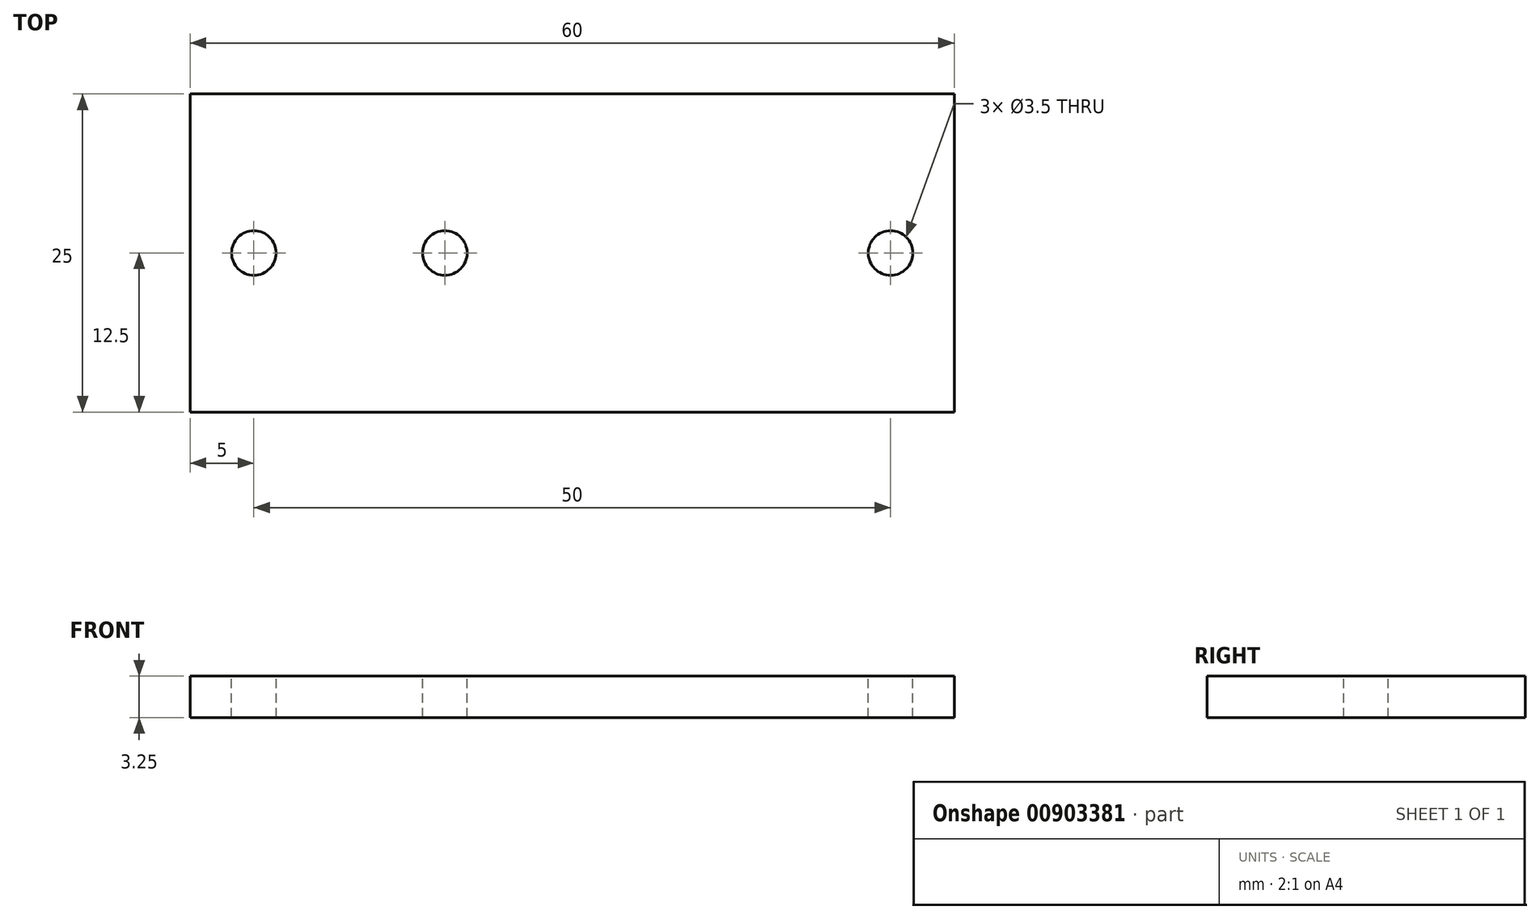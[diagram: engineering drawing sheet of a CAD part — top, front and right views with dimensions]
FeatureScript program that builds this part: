
annotation { "Feature Type Name" : "Feature", "Feature Type Description" : "" }
export const myFeature = defineFeature(function(context is Context, id is Id, definition is map)
    precondition{}
    {
        {
            var Q0;
            Q0=qCreatedBy(makeId("Top.planeOp"), FACE);
            var sketch = newSketch(context, id + "F0", { "sketchPlane" : qUnion([Q0])});
            skLineSegment(sketch, "E0.bottom", {"start": v(0, 0) * mm, "end": v(60, 0) * mm});
            skLineSegment(sketch, "E0.top", {"start": v(0, 25) * mm, "end": v(60, 25) * mm});
            skLineSegment(sketch, "E0.left", {"start": v(0, 0) * mm, "end": v(0, 25) * mm});
            skLineSegment(sketch, "E0.right", {"start": v(60, 0) * mm, "end": v(60, 25) * mm});
            skLineSegment(sketch, "E1", {"start": v(60, 12.5) * mm, "end": v(0, 12.5) * mm, "construction": true});
            skCircle(sketch, "E2", {"center": v(5, 12.5) * mm, "radius": 1.75 * mm});
            skCircle(sketch, "E3", {"center": v(55, 12.5) * mm, "radius": 1.75 * mm});
            skCircle(sketch, "E4", {"center": v(20, 12.5) * mm, "radius": 1.75 * mm});
            skSolve(sketch);
        }
        {
            var Q0;
            Q0 = qSketchRegion(id + "F0", true);
            extrude(context, id + "F1", {"entities" : qUnion([Q0]), "oppositeDirection" : true, "depth" : 3.25 * mm, "offsetDistance" : 25 * mm});
        }
    });
